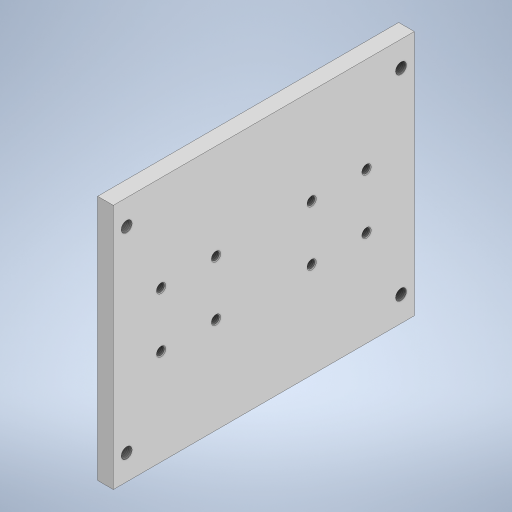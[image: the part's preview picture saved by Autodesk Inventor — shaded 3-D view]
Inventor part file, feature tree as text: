
AUTODESK INVENTOR PART (.ipt)
format: ipt  version: 2023.5 (Build 275446000, 446)  size: 276,992 bytes
history: native  units: mm
features: sketch x4, thread x4, extrude x2, chamfer x2, hole x1
ambient origin geometry x8: Origin, YZ Plane, XZ Plane, XY Plane, X Axis, Y Axis, Z Axis, Center Point
bodies: Volumenkörper1 (feature_tree)
feature tree (13):
  extrude  "Extrusion1"  Depth=157.0mm
  sketch  "草图5"  dims[d2=78.5mm d3=96.0mm d4=10.0mm d5=0.0mm]
  hole  "孔1"  [1 undecoded]
  chamfer  "倒角1"  Distance=10.0mm
  extrude  "拉伸5"  Depth=48.0mm
  thread  "螺纹6"  [1 undecoded]
  thread  "螺纹7"  [1 undecoded]
  thread  "螺纹8"  [1 undecoded]
  thread  "螺纹9"  [1 undecoded]
  chamfer  "倒角4"  Distance=40.0mm Angle=360.0deg
  sketch  "Skizze1"  dims[d0=192.0mm d1=157.0mm]
  sketch  "草图6"  dims[d31=50.0mm d32=48.0mm d33=24.0mm d34=35.0mm d35=35.0mm d36=5.0mm d37=40.0mm d39=360.0deg]
  sketch  "草图10"  dims[d41=4.917mm d42=12.0mm d43=4.0mm d44=2.0mm d45=90.0deg d46=8.0mm d47=20.594885mm d48=5.0mm d49=5.0mm d50=5.0mm d51=5.0mm d52=0.5mm d53=2.0mm d54=45.0deg d74=96.0mm d75=175.0mm d76=125.0mm d77=6.5mm d78=10.0mm d79=0.0mm d80=10.0mm d81=0.0mm d82=10.0mm d83=0.0mm d84=10.0mm d85=0.0mm d86=10.0mm d87=0.0mm d88=0.2mm d89=2.0mm d90=45.0deg d55=0.75mm d56=20.594885mm d57=0.0625mm d58=0.75mm d59=0.375mm]
note: 5 required parameter values undecoded (feature->parameter linkage not recoverable at this tier; creation-order binding heuristic only, values carry confidence <= 0.55)
